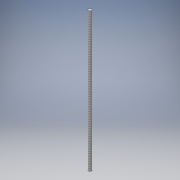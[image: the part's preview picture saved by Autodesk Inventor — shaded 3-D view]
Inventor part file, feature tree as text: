
AUTODESK INVENTOR PART (.ipt)
format: ipt  version: 2019 (Build 230136000, 136)  size: 92,672 bytes
history: native  units: in
note: dims shown in document units (in); Inventor stores cm internally (conversion verified against a paired STEP export)
features: extrude x1, thread x1, sketch x1
ambient origin geometry x8: Origin, YZ Plane, XZ Plane, XY Plane, X Axis, Y Axis, Z Axis, Center Point
bodies: Solid1 (feature_tree)
feature tree (3):
  extrude  "Extrusion1"  Depth=16.0in TaperAngle=0.0deg
  thread  "Thread1"  [1 undecoded]
  sketch  "Sketch1"  dims[d0=0.35in d1=16.0in d2=0.0in d3=1.0in d4=0.0in]
note: 1 required parameter value undecoded (feature->parameter linkage not recoverable at this tier; creation-order binding heuristic only, values carry confidence <= 0.55)
